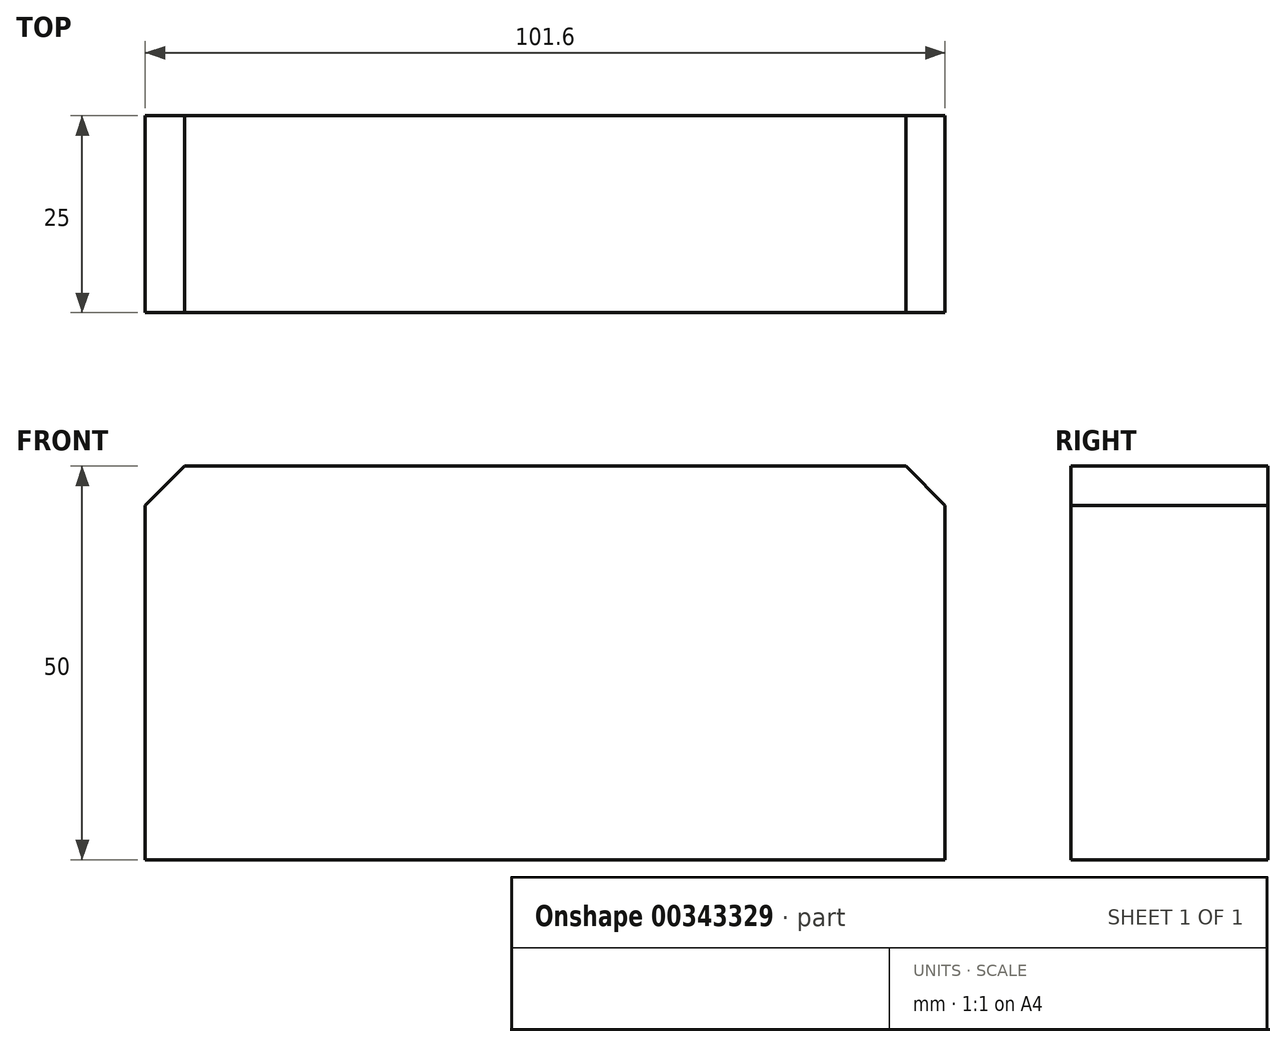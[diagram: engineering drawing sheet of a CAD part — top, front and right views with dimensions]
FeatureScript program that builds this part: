
annotation { "Feature Type Name" : "Feature", "Feature Type Description" : "" }
export const myFeature = defineFeature(function(context is Context, id is Id, definition is map)
    precondition{}
    {
        {
            var Q0;
            Q0=qCreatedBy(makeId("Front.planeOp"),FACE);
            var sketch = newSketch(context, id + "F0", { "sketchPlane" : qUnion([Q0])});
            skLineSegment(sketch, "E0.bottom", {"start": v(-50, 25) * mm, "end": v(51.6, 25) * mm});
            skLineSegment(sketch, "E0.top", {"start": v(-50, -25) * mm, "end": v(51.6, -25) * mm});
            skLineSegment(sketch, "E0.left", {"start": v(-50, 25) * mm, "end": v(-50, -25) * mm});
            skLineSegment(sketch, "E0.right", {"start": v(51.6, 25) * mm, "end": v(51.6, -25) * mm});
            skSolve(sketch);
        }
        {
            var Q0;
            Q0 = qSketchRegion(id + "F0", true);
            extrude(context, id + "F1", {"entities" : qUnion([Q0]), "depth" : 25 * mm});
        }
        {
            var Q0;
            Q0=makeQuery(id+"F1.opExtrude","SWEPT_EDGE",EDGE,{"disambiguationData":[OSD([sQuery(id+"F0.wireOp",EDGE,"E0.bottom"),sQuery(id+"F0.wireOp",EDGE,"E0.left")])]});
            var Q1;
            Q1=makeQuery(id+"F1.opExtrude","SWEPT_EDGE",EDGE,{"disambiguationData":[OSD([sQuery(id+"F0.wireOp",EDGE,"E0.bottom"),sQuery(id+"F0.wireOp",EDGE,"E0.right")])]});
            chamfer(context, id + "F2", {"entities" : qUnion([Q0, Q1]), "width" : 5 * mm, "tangentPropagation" : true});
        }
    });
